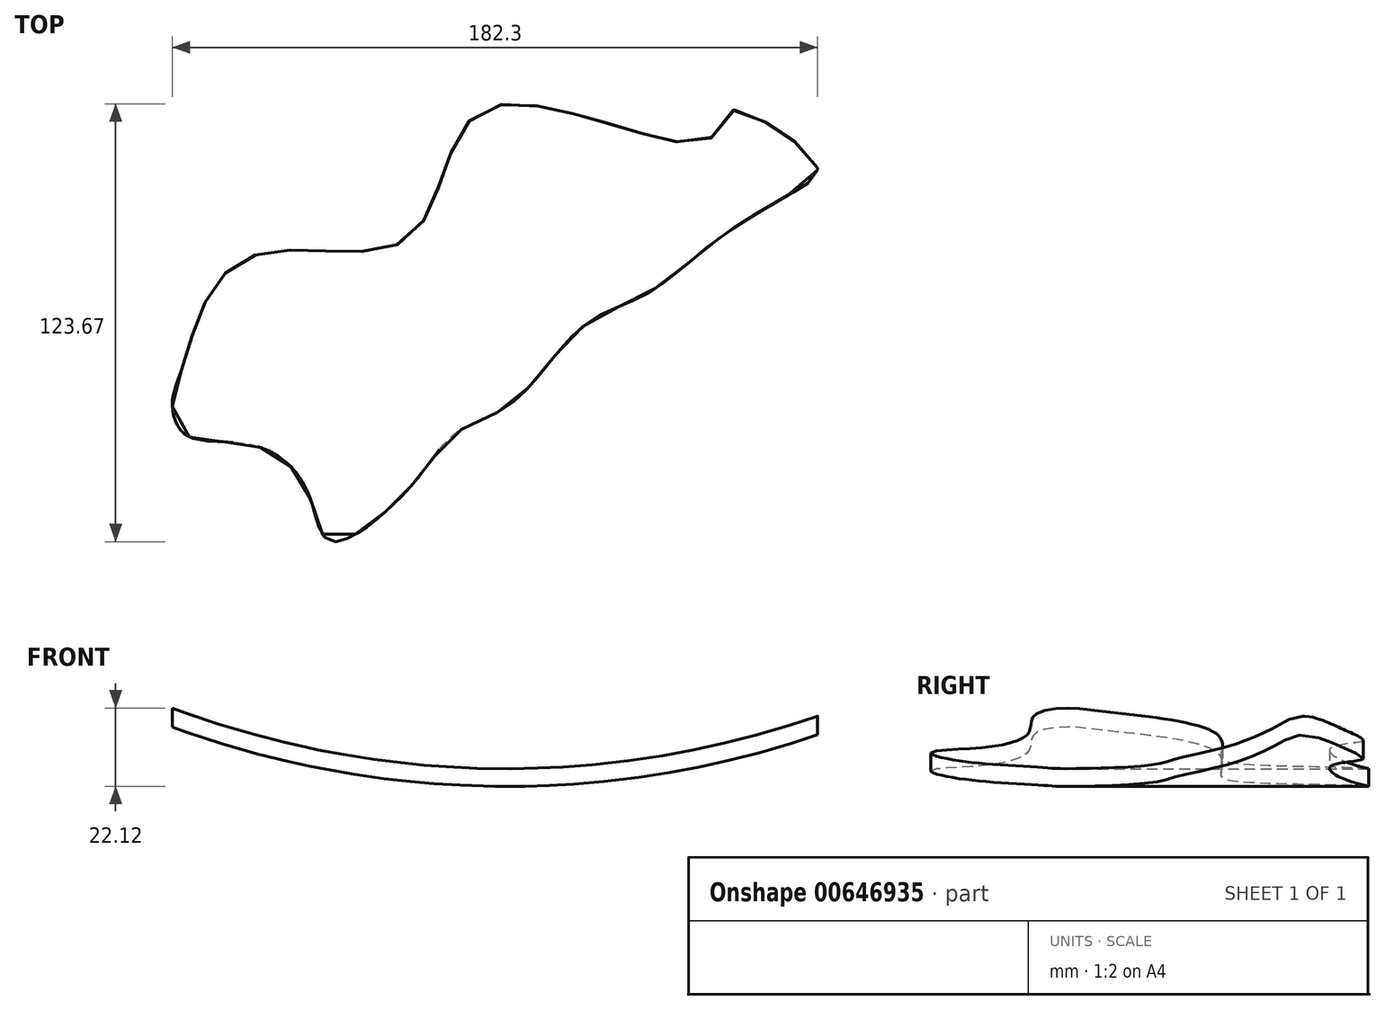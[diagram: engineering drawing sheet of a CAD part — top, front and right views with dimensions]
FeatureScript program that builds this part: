
annotation { "Feature Type Name" : "Feature", "Feature Type Description" : "" }
export const myFeature = defineFeature(function(context is Context, id is Id, definition is map)
    precondition{}
    {
        {
            var Q0;
            Q0=qCreatedBy(makeId("Top.planeOp"),FACE);
            var sketch = newSketch(context, id + "F0", { "sketchPlane" : qUnion([Q0])});
            skText(sketch, "E0", { "text": "M", "fontName": "OpenSans-Bold.ttf"});
            skLineSegment(sketch, "E1", {"start": v(-58.02, 23) * mm, "end": v(-20.46, 52.47) * mm, "construction": true});
            skLineSegment(sketch, "E2", {"start": v(-58.02, 52.47) * mm, "end": v(-20.46, 23) * mm, "construction": true});
            skPoint(sketch, "E3", {"position": v(-62.42, 35.92) * mm});
            skPoint(sketch, "E4", {"position": v(-39.24, 37.73) * mm});
            skCircle(sketch, "E5", {"center": v(-39.24, 37.73) * mm, "radius": 27.62 * mm});
            const initialGuessF0  = {"E0": [-0.05802, 0.023, 1, 0, 0.02946]};
            skSetInitialGuess(sketch, initialGuessF0);
            skSolve(sketch);
        }
        {
            var Q0;
            Q0=makeQuery(id+"F0.imprint","IMPRINT",FACE,{"disambiguationData":[TD([[makeQuery(id+"F0.imprint","IMPRINT",EDGE,{"derivedFrom":sQuery(id+"F0.wireOp",EDGE,"E0.sketch_text.stroke-0")}),1.0]])]});
            extrude(context, id + "F1", {"entities" : qUnion([Q0]), "depth" : 1 * mm, "offsetDistance" : 25 * mm});
        }
        {
            var Q0;
            Q0=makeQuery(id+"F0.imprint","IMPRINT",FACE,{"disambiguationData":[TD([[makeQuery(id+"F0.imprint","IMPRINT",EDGE,{"derivedFrom":sQuery(id+"F0.wireOp",EDGE,"E0.sketch_text.stroke-0")}),-1.0]])]});
            extrude(context, id + "F2", {"entities" : qUnion([Q0]), "depth" : 1 * mm, "offsetDistance" : 25 * mm});
        }
        {
            var Q0;
            Q0=qCreatedBy(makeId("Top.planeOp"),FACE);
            var sketch = newSketch(context, id + "F3", { "sketchPlane" : qUnion([Q0])});
            skFitSpline(sketch, "E6", {"points": [v(-179.72, -113.4) * mm, v(-182.28, -122.34) * mm, v(-178.45, -131.62) * mm, v(-159.58, -134.5) * mm, v(-143.92, -147.92) * mm, v(-137.52, -161.67) * mm, v(-114.5, -145.68) * mm, v(-102.04, -130.98) * mm, v(-86.37, -122.66) * mm, v(-66.23, -100.93) * mm, v(-48.65, -91.97) * mm, v(-29.79, -77.59) * mm, v(-8.69, -64.16) * mm, v(0, -56.17) * mm, v(-14.12, -43.7) * mm, v(-24.35, -40.18) * mm, v(-32.34, -48.81) * mm, v(-93.73, -39.54) * mm, v(-115.46, -75.99) * mm, v(-162.14, -82.06) * mm, v(-179.72, -113.4) * mm]});
            skSolve(sketch);
        }
        {
            var Q0;
            Q0=makeQuery(id+"F3.imprint","IMPRINT",FACE,{"disambiguationData":[TD([[makeQuery(id+"F3.imprint","IMPRINT",EDGE,{"derivedFrom":sQuery(id+"F3.wireOp",EDGE,"E6")}),1.0]])]});
            extrude(context, id + "F4", {"entities" : qUnion([Q0]), "depth" : 100 * mm, "offsetDistance" : 25 * mm});
        }
        {
            var Q0;
            Q0=qCreatedBy(makeId("Front.planeOp"),FACE);
            var sketch = newSketch(context, id + "F5", { "sketchPlane" : qUnion([Q0])});
            skArc(sketch, "E7", {"start": v(-195.8, 73.86) * mm, "mid": v(-98.63, 51.47) * mm, "end": v(0, 66.08) * mm});
            skArc(sketch, "E8.0", {"start": v(-197.8, 69.28) * mm, "mid": v(-98.7, 46.46) * mm, "end": v(1.89, 61.44) * mm});
            skLineSegment(sketch, "E9", {"start": v(-197.8, 69.28) * mm, "end": v(-195.8, 73.86) * mm});
            skLineSegment(sketch, "E10", {"start": v(1.89, 61.44) * mm, "end": v(0, 66.08) * mm});
            skSolve(sketch);
        }
        {
            var Q0;
            Q0=makeQuery(id+"F5.imprint","IMPRINT",FACE,{"disambiguationData":[TD([[makeQuery(id+"F5.imprint","IMPRINT",EDGE,{"derivedFrom":sQuery(id+"F5.wireOp",EDGE,"E7")}),-1.0]])]});
            extrude(context, id + "F6", {"entities" : qUnion([Q0]), "operationType" : NewBodyOperationType.INTERSECT, "depth" : 195 * mm, "offsetDistance" : 25 * mm});
        }
    });
